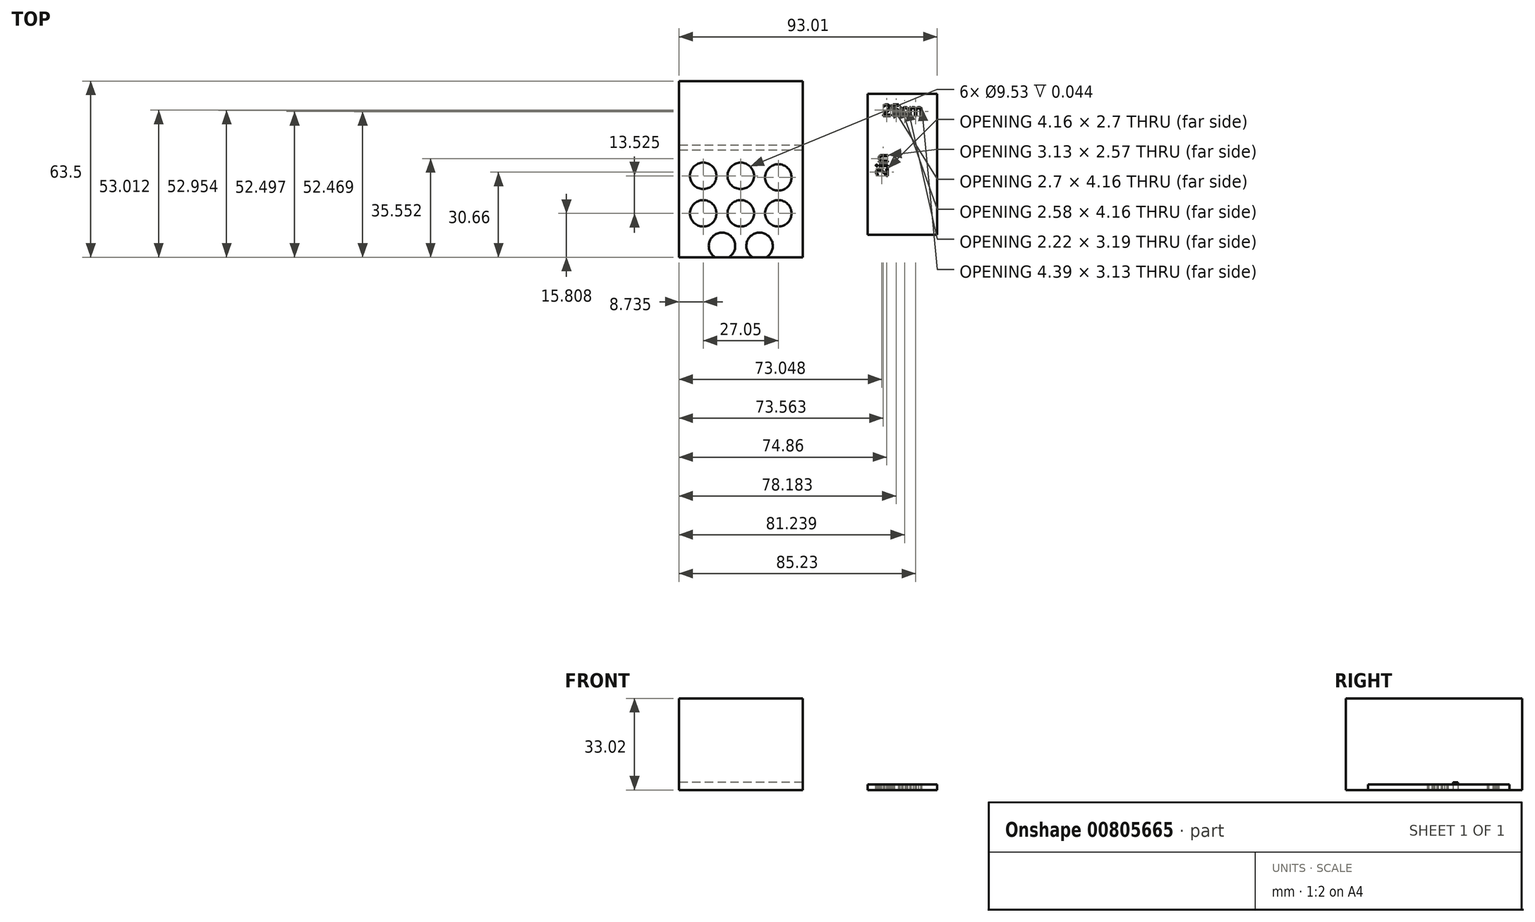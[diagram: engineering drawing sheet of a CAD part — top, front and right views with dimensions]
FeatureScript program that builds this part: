
annotation { "Feature Type Name" : "Feature", "Feature Type Description" : "" }
export const myFeature = defineFeature(function(context is Context, id is Id, definition is map)
    precondition{}
    {
        {
            var Q0;
            Q0=qCreatedBy(makeId("Top.planeOp"),FACE);
            var sketch = newSketch(context, id + "F0", { "sketchPlane" : qUnion([Q0])});
            skLineSegment(sketch, "E0.bottom", {"start": v(22.26, -31.75) * mm, "end": v(-22.26, -31.75) * mm});
            skLineSegment(sketch, "E0.top", {"start": v(22.26, 31.75) * mm, "end": v(-22.26, 31.75) * mm});
            skLineSegment(sketch, "E0.left", {"start": v(22.26, -31.75) * mm, "end": v(22.26, 31.75) * mm});
            skLineSegment(sketch, "E0.right", {"start": v(-22.26, -31.75) * mm, "end": v(-22.26, 31.75) * mm});
            skPoint(sketch, "E0.middle", {"position": v(0, 0) * mm});
            skSolve(sketch);
        }
        {
            var Q0;
            Q0=makeQuery(id+"F0.imprint","IMPRINT",FACE,{"disambiguationData":[TD([[makeQuery(id+"F0.imprint","IMPRINT",EDGE,{"derivedFrom":sQuery(id+"F0.wireOp",EDGE,"E0.bottom")}),-1.0]])]});
            extrude(context, id + "F1", {"entities" : qUnion([Q0]), "depth" : 33.02 * mm, "offsetDistance" : 25 * mm});
        }
        {
            var Q0;
            Q0=makeQuery(id+"F1.opExtrude","CAP_FACE",FACE,{"disambiguationData":[OSD([sQuery(id+"F0.wireOp",EDGE,"E0.bottom"),sQuery(id+"F0.wireOp",EDGE,"E0.top"),sQuery(id+"F0.wireOp",EDGE,"E0.left"),sQuery(id+"F0.wireOp",EDGE,"E0.right")])],"isStart":true});
            var sketch = newSketch(context, id + "F2", { "sketchPlane" : qUnion([Q0])});
            skLineSegment(sketch, "E1", {"start": v(22.26, -8.61) * mm, "end": v(-22.26, -8.61) * mm});
            skLineSegment(sketch, "E2", {"start": v(22.26, -6.83) * mm, "end": v(-22.26, -6.83) * mm});
            skLineSegment(sketch, "E3", {"start": v(22.26, -8.61) * mm, "end": v(22.26, -6.83) * mm});
            skLineSegment(sketch, "E4", {"start": v(-22.26, -8.61) * mm, "end": v(-22.26, -6.83) * mm});
            skSolve(sketch);
        }
        {
            var Q0;
            Q0 = qSketchRegion(id + "F2", true);
            extrude(context, id + "F3", {"entities" : qUnion([Q0]), "operationType" : NewBodyOperationType.REMOVE, "oppositeDirection" : true, "depth" : 2.77 * mm, "offsetDistance" : 25 * mm});
        }
        {
            var Q0;
            Q0=makeQuery(id+"F1.opExtrude","CAP_FACE",FACE,{"disambiguationData":[OSD([sQuery(id+"F0.wireOp",EDGE,"E0.bottom"),sQuery(id+"F0.wireOp",EDGE,"E0.top"),sQuery(id+"F0.wireOp",EDGE,"E0.left"),sQuery(id+"F0.wireOp",EDGE,"E0.right")])],"isStart":false});
            var sketch = newSketch(context, id + "F4", { "sketchPlane" : qUnion([Q0])});
            skCircle(sketch, "E5", {"center": v(0, -15.94) * mm, "radius": 4.76 * mm});
            skCircle(sketch, "E6", {"center": v(-13.52, -15.94) * mm, "radius": 4.76 * mm});
            skLineSegment(sketch, "E7", {"start": v(0, 0) * mm, "end": v(0, -7.4) * mm, "construction": true});
            skCircle(sketch, "E8.MirrorC", {"center": v(13.52, -15.94) * mm, "radius": 4.76 * mm});
            skCircle(sketch, "E9", {"center": v(-6.76, -27.66) * mm, "radius": 4.76 * mm});
            skCircle(sketch, "E10.MirrorC", {"center": v(6.76, -27.66) * mm, "radius": 4.76 * mm});
            skLineSegment(sketch, "E11", {"start": v(0, -15.94) * mm, "end": v(6.2, -15.94) * mm, "construction": true});
            skLineSegment(sketch, "E12.0", {"start": v(22.26, 8.61) * mm, "end": v(-22.26, 8.61) * mm, "construction": true});
            skLineSegment(sketch, "E13.0", {"start": v(22.26, 6.83) * mm, "end": v(-22.26, 6.83) * mm, "construction": true});
            skLineSegment(sketch, "E14", {"start": v(-22.26, -16.03) * mm, "end": v(22.26, -16.03) * mm, "construction": true});
            skCircle(sketch, "E15", {"center": v(0, -2.42) * mm, "radius": 4.76 * mm});
            skCircle(sketch, "E16", {"center": v(-13.52, -2.42) * mm, "radius": 4.76 * mm});
            skCircle(sketch, "E17.MirrorC", {"center": v(13.52, -2.98) * mm, "radius": 4.76 * mm});
            skLineSegment(sketch, "E18", {"start": v(0, -2.42) * mm, "end": v(6.2, -2.42) * mm, "construction": true});
            skSolve(sketch);
        }
        {
            var Q0;
            Q0 = qSketchRegion(id + "F4", true);
            extrude(context, id + "F5", {"entities" : qUnion([Q0]), "operationType" : NewBodyOperationType.REMOVE, "oppositeDirection" : true, "depth" : 3 / 203.2 * mm * 3, "offsetDistance" : 25 * mm});
        }
        {
            var Q0;
            Q0=qCreatedBy(makeId("Top.planeOp"),FACE);
            var sketch = newSketch(context, id + "F6", { "sketchPlane" : qUnion([Q0])});
            skLineSegment(sketch, "E19.bottom", {"start": v(45.75, 27.1) * mm, "end": v(70.75, 27.1) * mm});
            skLineSegment(sketch, "E19.top", {"start": v(45.75, -23.7) * mm, "end": v(70.75, -23.7) * mm});
            skLineSegment(sketch, "E19.left", {"start": v(45.75, 27.1) * mm, "end": v(45.75, -23.7) * mm});
            skLineSegment(sketch, "E19.right", {"start": v(70.75, 27.1) * mm, "end": v(70.75, -23.7) * mm});
            skText(sketch, "E20", { "text": "2in\n", "fontName": "OpenSans-Regular.ttf"});
            skText(sketch, "E21", { "text": "25cm", "fontName": "OpenSans-Regular.ttf"});
            skPoint(sketch, "E22", {"position": v(58.25, 27.1) * mm});
            skPoint(sketch, "E23", {"position": v(45.75, 1.7) * mm});
            const initialGuessF6  = {"E20": [0.05287, -0.00272, 0, 1, 0.00414], "E21": [0.05097, 0.01918, 1, 0, 0.00414]};
            skSetInitialGuess(sketch, initialGuessF6);
            skSolve(sketch);
        }
        {
            var Q0;
            Q0=makeQuery(id+"F6.imprint","IMPRINT",FACE,{"disambiguationData":[TD([[makeQuery(id+"F6.imprint","IMPRINT",EDGE,{"derivedFrom":sQuery(id+"F6.wireOp",EDGE,"E19.bottom")}),-1.0]])]});
            extrude(context, id + "F7", {"entities" : qUnion([Q0]), "depth" : 2 * mm, "offsetDistance" : 25 * mm});
        }
    });
